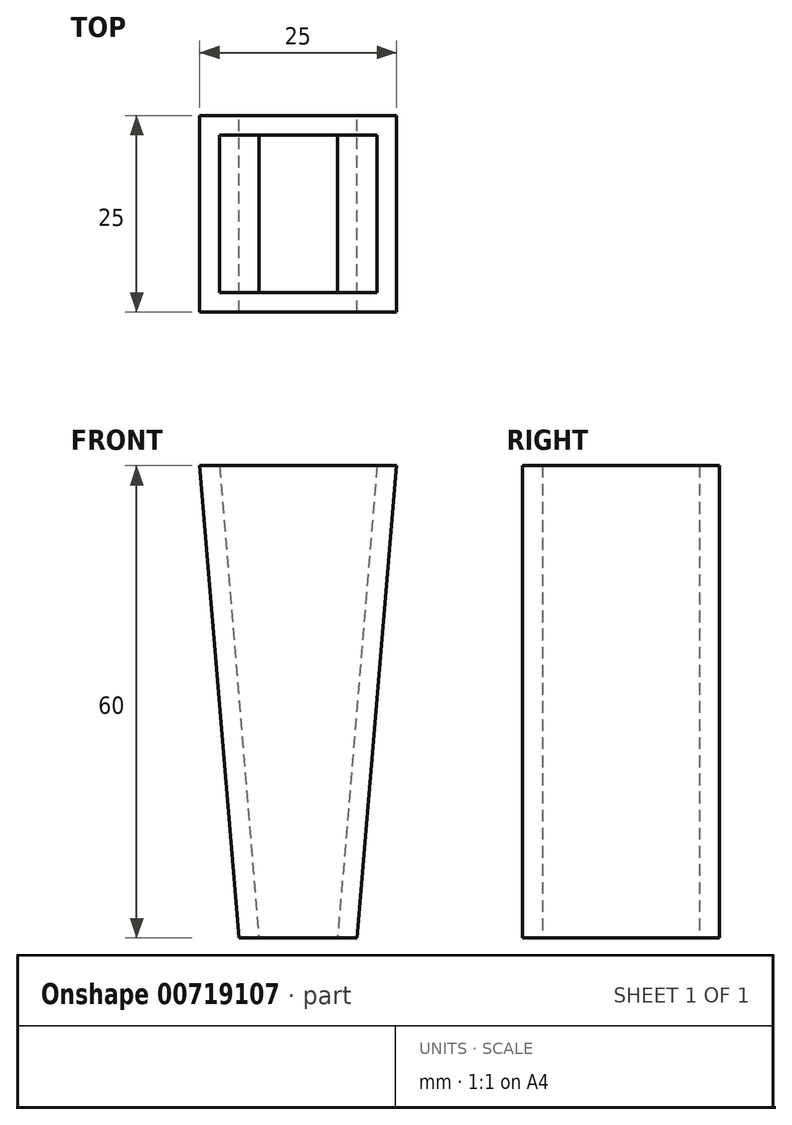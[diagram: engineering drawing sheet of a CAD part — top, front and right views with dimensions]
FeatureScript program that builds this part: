
annotation { "Feature Type Name" : "Feature", "Feature Type Description" : "" }
export const myFeature = defineFeature(function(context is Context, id is Id, definition is map)
    precondition{}
    {
        {
            var Q0;
            Q0=qCreatedBy(makeId("Front.planeOp"),FACE);
            var sketch = newSketch(context, id + "F0", { "sketchPlane" : qUnion([Q0])});
            skLineSegment(sketch, "E0", {"start": v(-12.5, 0) * mm, "end": v(-7.5, -60) * mm});
            skLineSegment(sketch, "E1.MirrorCS", {"start": v(12.5, 0) * mm, "end": v(7.5, -60) * mm});
            skLineSegment(sketch, "E2", {"start": v(-7.5, -60) * mm, "end": v(7.5, -60) * mm});
            skLineSegment(sketch, "E3", {"start": v(-12.5, 0) * mm, "end": v(12.5, 0) * mm});
            skSolve(sketch);
        }
        {
            var Q0;
            Q0 = qSketchRegion(id + "F0", true);
            extrude(context, id + "F1", {"entities" : qUnion([Q0]), "depth" : 25 * mm, "offsetDistance" : 25 * mm});
        }
        {
            var Q0;
            Q0=makeQuery(id+"F1.opExtrude","SWEPT_FACE",FACE,{"disambiguationData":[OSD([sQuery(id+"F0.wireOp",EDGE,"E2")])]});
            var Q1;
            Q1=makeQuery(id+"F1.opExtrude","SWEPT_FACE",FACE,{"disambiguationData":[OSD([sQuery(id+"F0.wireOp",EDGE,"E3")])]});
            shell(context, id + "F2", {"entities" : qUnion([Q0, Q1]), "thickness" : 2.5 * mm});
        }
    });
